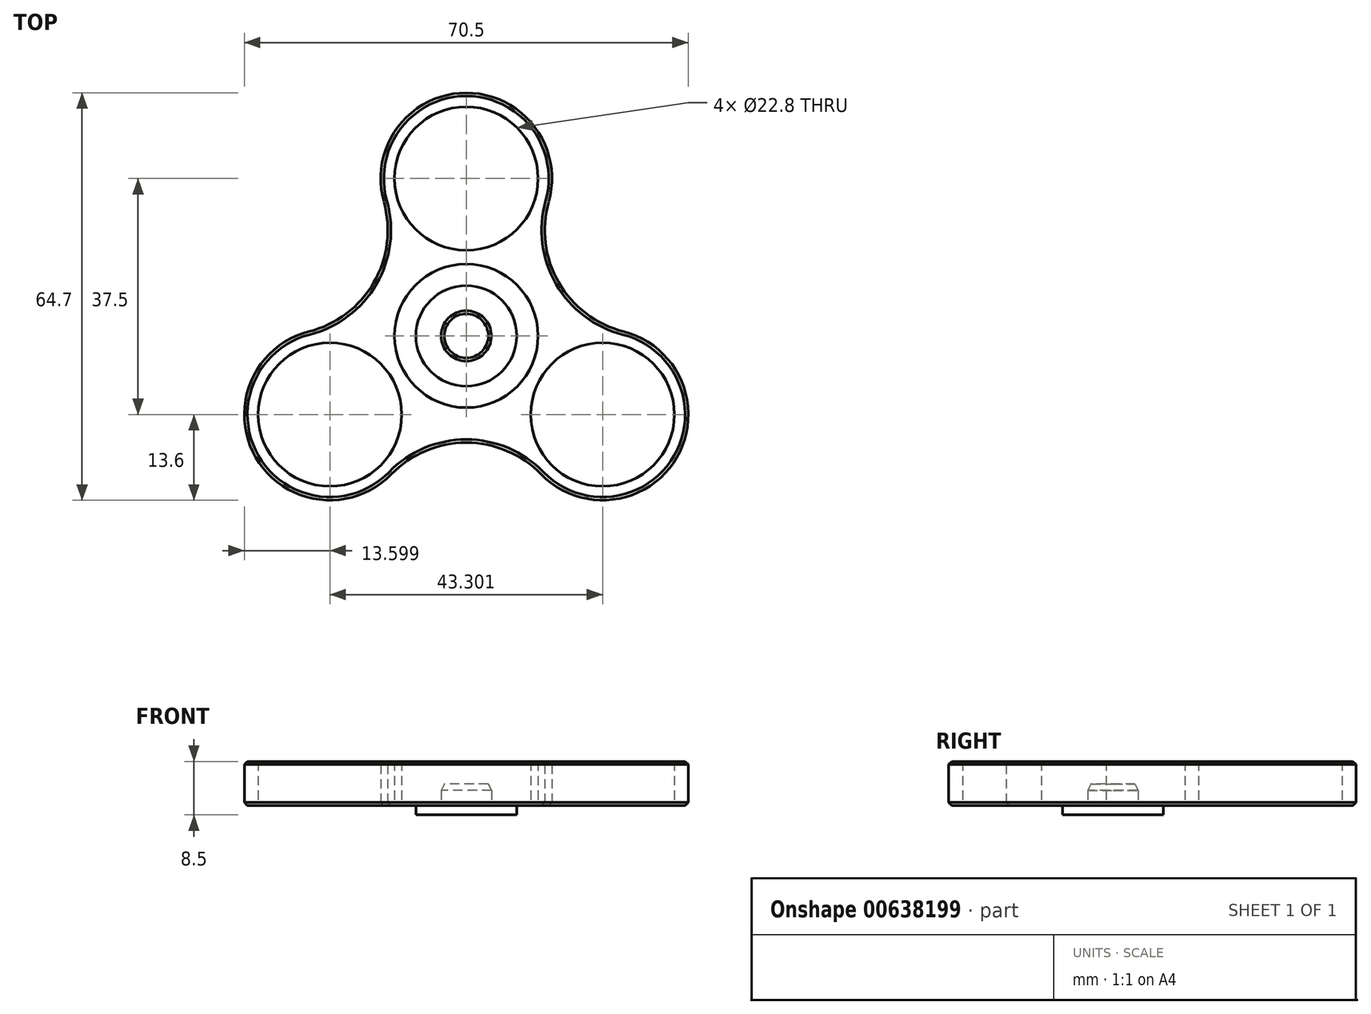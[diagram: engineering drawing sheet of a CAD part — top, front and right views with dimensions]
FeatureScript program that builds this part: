
annotation { "Feature Type Name" : "Feature", "Feature Type Description" : "" }
export const myFeature = defineFeature(function(context is Context, id is Id, definition is map)
    precondition{}
    {
        {
            var Q0;
            Q0=qCreatedBy(makeId("Top.planeOp"),FACE);
            var sketch = newSketch(context, id + "F0", { "sketchPlane" : qUnion([Q0])});
            skCircle(sketch, "E0", {"center": v(0, 0) * mm, "radius": 11.4 * mm});
            skLineSegment(sketch, "E1", {"start": v(0, 0) * mm, "end": v(0, 25) * mm, "construction": true});
            skLineSegment(sketch, "E2", {"start": v(-21.65, -12.5) * mm, "end": v(0, 0) * mm, "construction": true});
            skLineSegment(sketch, "E3", {"start": v(0, 0) * mm, "end": v(21.65, -12.5) * mm, "construction": true});
            skCircle(sketch, "E4", {"center": v(0, 25) * mm, "radius": 11.4 * mm});
            skCircle(sketch, "E5", {"center": v(-21.65, -12.5) * mm, "radius": 11.4 * mm});
            skCircle(sketch, "E6", {"center": v(21.65, -12.5) * mm, "radius": 11.4 * mm});
            skLineSegment(sketch, "E7", {"start": v(0, 25) * mm, "end": v(-21.65, -12.5) * mm, "construction": true});
            skLineSegment(sketch, "E8", {"start": v(-21.65, -12.5) * mm, "end": v(21.65, -12.5) * mm, "construction": true});
            skLineSegment(sketch, "E9", {"start": v(21.65, -12.5) * mm, "end": v(0, 25) * mm, "construction": true});
            skLineSegment(sketch, "E10", {"start": v(0, 0) * mm, "end": v(21.65, 12.5) * mm, "construction": true});
            skLineSegment(sketch, "E11", {"start": v(0, 0) * mm, "end": v(-21.65, 12.5) * mm, "construction": true});
            skLineSegment(sketch, "E12", {"start": v(0, 0) * mm, "end": v(0, -25) * mm, "construction": true});
            skLineSegment(sketch, "E13", {"start": v(13.09, 21.3) * mm, "end": v(8.44, 4.88) * mm, "construction": true});
            skLineSegment(sketch, "E14", {"start": v(25, 0.68) * mm, "end": v(8.44, 4.88) * mm, "construction": true});
            skLineSegment(sketch, "E15", {"start": v(-13.09, 21.3) * mm, "end": v(-8.44, 4.88) * mm, "construction": true});
            skLineSegment(sketch, "E16", {"start": v(-8.44, 4.88) * mm, "end": v(-25, 0.68) * mm, "construction": true});
            skLineSegment(sketch, "E17", {"start": v(-11.9, -21.98) * mm, "end": v(0, -9.75) * mm, "construction": true});
            skPoint(sketch, "E17.endSnap0", {"position": v(0, -12.5) * mm});
            skLineSegment(sketch, "E18", {"start": v(0, -9.75) * mm, "end": v(11.9, -21.98) * mm, "construction": true});
            skLineSegment(sketch, "E19", {"start": v(21.65, -12.5) * mm, "end": v(11.9, -21.98) * mm, "construction": true});
            skLineSegment(sketch, "E20", {"start": v(11.9, -21.98) * mm, "end": v(11.9, -21.98) * mm});
            skArc(sketch, "E21", {"start": v(11.9, -21.98) * mm, "mid": v(0, -16.96) * mm, "end": v(-11.9, -21.98) * mm});
            skCircle(sketch, "E22", {"center": v(0, 0) * mm, "radius": 33.57 * mm, "construction": true});
            skLineSegment(sketch, "E23", {"start": v(21.65, 12.5) * mm, "end": v(29.07, 16.78) * mm, "construction": true});
            skLineSegment(sketch, "E24", {"start": v(-21.65, 12.5) * mm, "end": v(-29.07, 16.78) * mm, "construction": true});
            skArc(sketch, "E25", {"start": v(-25, 0.68) * mm, "mid": v(-14.69, 8.48) * mm, "end": v(-13.09, 21.3) * mm});
            skArc(sketch, "E26", {"start": v(13.09, 21.3) * mm, "mid": v(14.69, 8.48) * mm, "end": v(25, 0.68) * mm});
            skArc(sketch, "E27", {"start": v(-13.09, 21.3) * mm, "mid": v(0, 11.4) * mm, "end": v(13.09, 21.3) * mm, "construction": true});
            skArc(sketch, "E28", {"start": v(13.09, 21.3) * mm, "mid": v(0, 38.6) * mm, "end": v(-13.09, 21.3) * mm});
            skArc(sketch, "E29", {"start": v(-25, 0.68) * mm, "mid": v(-33.43, -19.3) * mm, "end": v(-11.9, -21.98) * mm});
            skArc(sketch, "E30", {"start": v(-11.9, -21.98) * mm, "mid": v(-9.87, -5.7) * mm, "end": v(-25, 0.68) * mm, "construction": true});
            skArc(sketch, "E31", {"start": v(11.9, -21.98) * mm, "mid": v(21.65, -12.5) * mm, "end": v(25, 0.68) * mm, "construction": true});
            skArc(sketch, "E32", {"start": v(25, 0.68) * mm, "mid": v(-21.65, 12.5) * mm, "end": v(11.9, -21.98) * mm, "construction": true});
            skLineSegment(sketch, "E33", {"start": v(11.9, -21.98) * mm, "end": v(0, -33.57) * mm, "construction": true});
            skLineSegment(sketch, "E34", {"start": v(25, 0.68) * mm, "end": v(25, 0.68) * mm});
            skArc(sketch, "E35", {"start": v(25, 0.68) * mm, "mid": v(9.87, -5.7) * mm, "end": v(11.9, -21.98) * mm, "construction": true});
            skArc(sketch, "E36", {"start": v(11.9, -21.98) * mm, "mid": v(33.43, -19.3) * mm, "end": v(25, 0.68) * mm});
            skSolve(sketch);
        }
        {
            var Q0;
            Q0=makeQuery(id+"F0.imprint","IMPRINT",FACE,{"disambiguationData":[TD([[makeQuery(id+"F0.imprint","IMPRINT",EDGE,{"derivedFrom":sQuery(id+"F0.wireOp",EDGE,"E0")}),-1.0]])]});
            extrude(context, id + "F1", {"entities" : qUnion([Q0]), "depth" : 7 * mm, "offsetDistance" : 25 * mm});
        }
        {
            var Q0;
            Q0=qCreatedBy(makeId("Top.planeOp"),FACE);
            var sketch = newSketch(context, id + "F2", { "sketchPlane" : qUnion([Q0])});
            skCircle(sketch, "E37", {"center": v(0, 0) * mm, "radius": 8 * mm});
            skCircle(sketch, "E38", {"center": v(0, 0) * mm, "radius": 4 * mm});
            skSolve(sketch);
        }
        {
            var Q0;
            Q0=makeQuery(id+"F2.imprint","IMPRINT",FACE,{"disambiguationData":[TD([[makeQuery(id+"F2.imprint","IMPRINT",EDGE,{"derivedFrom":sQuery(id+"F2.wireOp",EDGE,"E37")}),1.0]])]});
            var Q1;
            Q1=makeQuery(id+"F2.imprint","IMPRINT",FACE,{"disambiguationData":[TD([[makeQuery(id+"F2.imprint","IMPRINT",EDGE,{"derivedFrom":sQuery(id+"F2.wireOp",EDGE,"E38")}),1.0]])]});
            extrude(context, id + "F3", {"entities" : qUnion([Q0, Q1]), "oppositeDirection" : true, "depth" : 1.5 * mm, "offsetDistance" : 25 * mm});
        }
        {
            var Q0;
            Q0=makeQuery(id+"F2.imprint","IMPRINT",FACE,{"disambiguationData":[TD([[makeQuery(id+"F2.imprint","IMPRINT",EDGE,{"derivedFrom":sQuery(id+"F2.wireOp",EDGE,"E38")}),1.0]])]});
            extrude(context, id + "F4", {"entities" : qUnion([Q0]), "operationType" : NewBodyOperationType.ADD, "depth" : 3.4 * mm, "offsetDistance" : 25 * mm});
        }
        {
            var Q0;
            Q0=makeQuery(id+"F4.opExtrude","CAP_EDGE",EDGE,{"disambiguationData":[OSD([sQuery(id+"F2.wireOp",EDGE,"E38")])],"isStart":false});
            chamfer(context, id + "F5", {"entities" : qUnion([Q0]), "chamferType" : ChamferType.TWO_OFFSETS, "width1" : 0.5 * mm, "oppositeDirection" : false, "width2" : 1 * mm, "tangentPropagation" : true});
        }
        {
            var Q0;
            Q0=makeQuery(id+"F1.opExtrude","CAP_EDGE",EDGE,{"disambiguationData":[OSD([sQuery(id+"F0.wireOp",EDGE,"E21")])],"isStart":true});
            var Q1;
            Q1=makeQuery(id+"F1.opExtrude","CAP_EDGE",EDGE,{"disambiguationData":[OSD([sQuery(id+"F0.wireOp",EDGE,"E21")])],"isStart":false});
            chamfer(context, id + "F6", {"entities" : qUnion([Q0, Q1]), "width" : 0.5 * mm, "tangentPropagation" : true});
        }
    });
